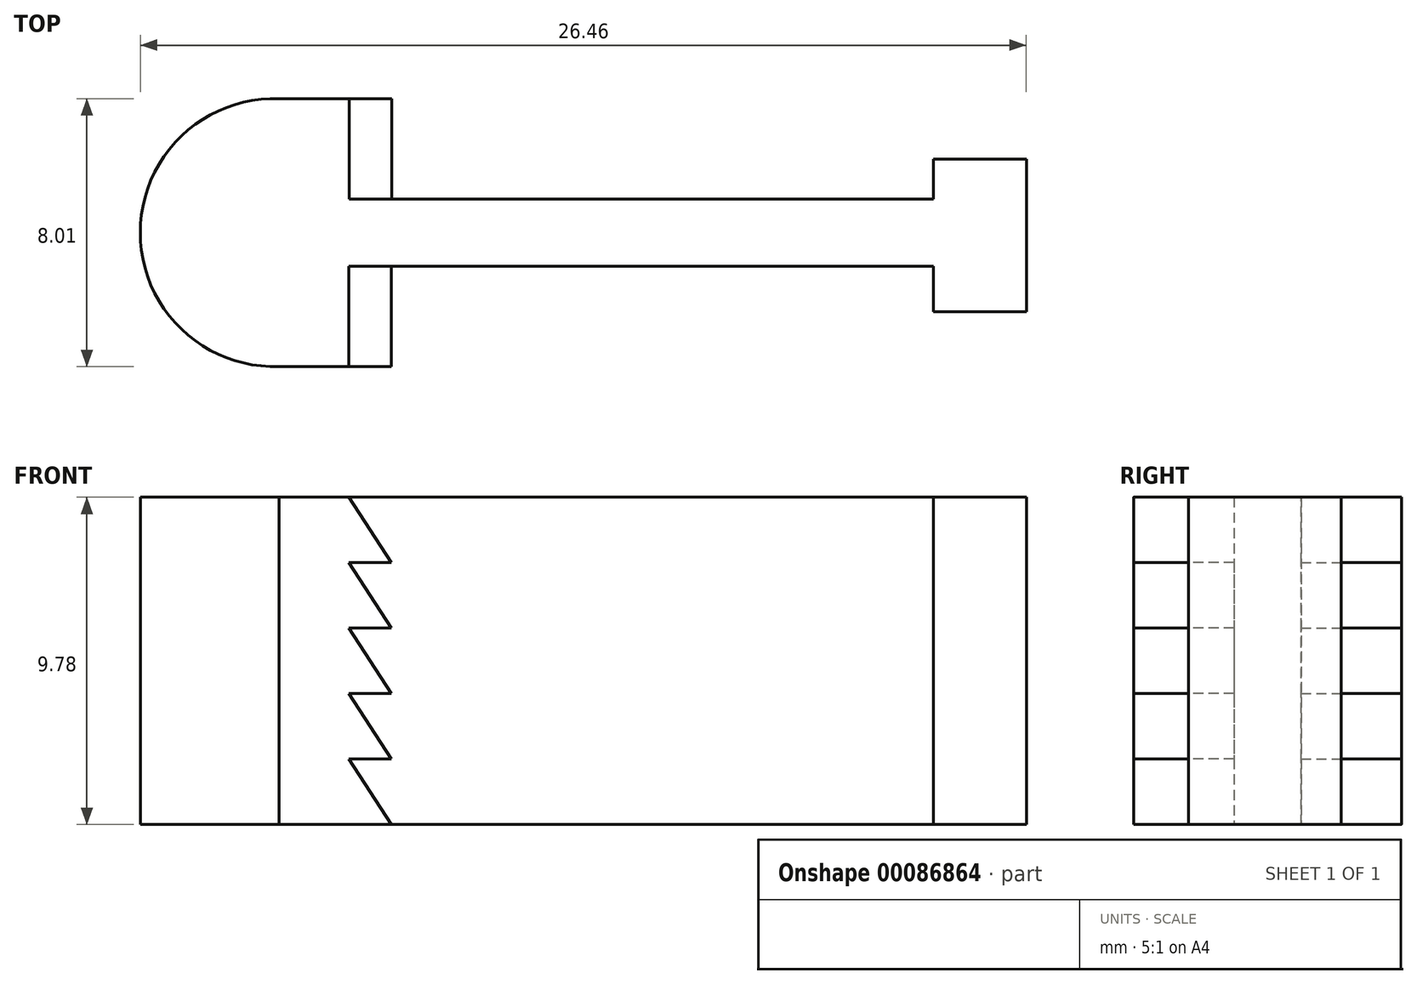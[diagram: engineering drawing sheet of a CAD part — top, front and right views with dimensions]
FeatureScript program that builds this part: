
annotation { "Feature Type Name" : "Feature", "Feature Type Description" : "" }
export const myFeature = defineFeature(function(context is Context, id is Id, definition is map)
    precondition{}
    {
        {
            var Q0;
            Q0=qCreatedBy(makeId("Top.planeOp"),FACE);
            var sketch = newSketch(context, id + "F0", { "sketchPlane" : qUnion([Q0])});
            skLineSegment(sketch, "E0.bottom", {"start": v(-4.73, -0.91) * mm, "end": v(13.05, -0.91) * mm});
            skLineSegment(sketch, "E0.top", {"start": v(-4.73, -2.91) * mm, "end": v(13.05, -2.91) * mm});
            skLineSegment(sketch, "E0.left", {"start": v(-4.73, -0.91) * mm, "end": v(-4.73, -2.91) * mm});
            skLineSegment(sketch, "E0.right", {"start": v(13.05, -0.91) * mm, "end": v(13.05, -2.91) * mm});
            skLineSegment(sketch, "E1.bottom", {"start": v(-4.73, -0.91) * mm, "end": v(-1.23, -0.91) * mm});
            skLineSegment(sketch, "E1.top", {"start": v(-4.73, 2.09) * mm, "end": v(-1.23, 2.09) * mm});
            skLineSegment(sketch, "E1.left", {"start": v(-4.73, -0.91) * mm, "end": v(-4.73, 2.09) * mm});
            skLineSegment(sketch, "E1.right", {"start": v(-1.23, -0.91) * mm, "end": v(-1.23, 2.09) * mm});
            skLineSegment(sketch, "E2.bottom", {"start": v(-4.73, -2.91) * mm, "end": v(-1.23, -2.91) * mm});
            skLineSegment(sketch, "E2.top", {"start": v(-4.73, -5.91) * mm, "end": v(-1.23, -5.91) * mm});
            skLineSegment(sketch, "E2.left", {"start": v(-4.73, -2.91) * mm, "end": v(-4.73, -5.91) * mm});
            skLineSegment(sketch, "E2.right", {"start": v(-1.23, -2.91) * mm, "end": v(-1.23, -5.91) * mm});
            skLineSegment(sketch, "E3.bottom", {"start": v(13.05, -0.91) * mm, "end": v(14.96, -0.91) * mm});
            skLineSegment(sketch, "E3.top", {"start": v(13.05, -2.91) * mm, "end": v(14.96, -2.91) * mm});
            skLineSegment(sketch, "E3.right", {"start": v(14.96, -0.91) * mm, "end": v(14.96, -2.91) * mm});
            skLineSegment(sketch, "E4.bottom", {"start": v(14.96, -4.27) * mm, "end": v(17.73, -4.27) * mm});
            skLineSegment(sketch, "E4.top", {"start": v(14.96, 0.29) * mm, "end": v(17.73, 0.29) * mm});
            skLineSegment(sketch, "E4.left", {"start": v(14.96, -4.27) * mm, "end": v(14.96, 0.29) * mm});
            skLineSegment(sketch, "E4.right", {"start": v(17.73, -4.27) * mm, "end": v(17.73, 0.29) * mm});
            skCircle(sketch, "E5", {"center": v(-4.73, -1.91) * mm, "radius": 4 * mm});
            skSolve(sketch);
        }
        {
            var Q0;
            {var subQ3=sQuery(id+"F0.wireOp",EDGE,"E4.bottom");Q0=makeQuery(id+"F0.imprint","IMPRINT",FACE,{"disambiguationData":[TD([[makeQuery(id+"F0.imprint","IMPRINT",EDGE,{"derivedFrom":subQ3}),1.0]])]});}
            var Q1;
            {var subQ0=sQuery(id+"F0.wireOp",EDGE,"E0.right");Q1=makeQuery(id+"F0.imprint","IMPRINT",FACE,{"disambiguationData":[TD([[makeQuery(id+"F0.imprint","IMPRINT",EDGE,{"derivedFrom":subQ0}),-1.0]])]});}
            var Q2;
            {var subQ0=sQuery(id+"F0.wireOp",EDGE,"E3.bottom");Q2=makeQuery(id+"F0.imprint","IMPRINT",FACE,{"disambiguationData":[TD([[makeQuery(id+"F0.imprint","IMPRINT",EDGE,{"derivedFrom":subQ0}),-1.0]])]});}
            var Q3;
            {var subQ1=sQuery(id+"F0.wireOp",EDGE,"E1.left");var subQ6=sQuery(id+"F0.wireOp",EDGE,"E1.top");var subQ9=makeQuery(id+"F0.imprint","INTERSECT",VERTEX,{"derivedFrom":[subQ6,subQ1]});Q3=makeQuery(id+"F0.imprint","IMPRINT",FACE,{"disambiguationData":[TD([[makeQuery(id+"F0.imprint","IMPRINT",EDGE,{"disambiguationData":[TD([[subQ9,-1.0]])],"derivedFrom":subQ6}),1.0]])]});}
            var Q4;
            {var subQ1=sQuery(id+"F0.wireOp",EDGE,"E2.left");var subQ6=sQuery(id+"F0.wireOp",EDGE,"E2.top");var subQ9=makeQuery(id+"F0.imprint","INTERSECT",VERTEX,{"derivedFrom":[subQ6,subQ1]});Q4=makeQuery(id+"F0.imprint","IMPRINT",FACE,{"disambiguationData":[TD([[makeQuery(id+"F0.imprint","IMPRINT",EDGE,{"disambiguationData":[TD([[subQ9,-1.0]])],"derivedFrom":subQ6}),-1.0]])]});}
            var Q5;
            {var subQ0=sQuery(id+"F0.wireOp",EDGE,"fi6eeUua-WoeC-Sxvv-xVol-Bu5kXO0VCXWT");var subQ1=sQuery(id+"F0.wireOp",EDGE,"E0.bottom");var subQ2=makeQuery(id+"F0.imprint","INTERSECT",VERTEX,{"derivedFrom":[subQ1,subQ0]});Q5=makeQuery(id+"F0.imprint","IMPRINT",FACE,{"disambiguationData":[TD([[makeQuery(id+"F0.imprint","IMPRINT",EDGE,{"disambiguationData":[TD([[subQ2,1.0]])],"derivedFrom":subQ1}),-1.0]])]});}
            var Q6;
            {var subQ0=sQuery(id+"F0.wireOp",EDGE,"E2.bottom");Q6=makeQuery(id+"F0.imprint","IMPRINT",FACE,{"disambiguationData":[TD([[makeQuery(id+"F0.imprint","IMPRINT",EDGE,{"derivedFrom":subQ0}),-1.0]])]});}
            var Q7;
            {var subQ0=sQuery(id+"F0.wireOp",EDGE,"E1.bottom");Q7=makeQuery(id+"F0.imprint","IMPRINT",FACE,{"disambiguationData":[TD([[makeQuery(id+"F0.imprint","IMPRINT",EDGE,{"derivedFrom":subQ0}),1.0]])]});}
            var Q8;
            Q8=makeQuery(id+"F0.imprint","IMPRINT",FACE,{"disambiguationData":[TD([[makeQuery(id+"F0.imprint","IMPRINT",EDGE,{"derivedFrom":sQuery(id+"F0.wireOp",EDGE,"E0.left")}),1.0]])]});
            var Q9;
            {var subQ0=sQuery(id+"F0.wireOp",EDGE,"fi6eeUua-WoeC-Sxvv-xVol-Bu5kXO0VCXWT");var subQ1=sQuery(id+"F0.wireOp",EDGE,"E2.left");var subQ2=makeQuery(id+"F0.imprint","INTERSECT",VERTEX,{"derivedFrom":[subQ1,subQ0]});Q9=makeQuery(id+"F0.imprint","IMPRINT",FACE,{"disambiguationData":[TD([[makeQuery(id+"F0.imprint","IMPRINT",EDGE,{"disambiguationData":[TD([[subQ2,1.0]])],"derivedFrom":subQ1}),-1.0]])]});}
            var Q10;
            {var subQ0=sQuery(id+"F0.wireOp",EDGE,"fi6eeUua-WoeC-Sxvv-xVol-Bu5kXO0VCXWT");var subQ1=sQuery(id+"F0.wireOp",EDGE,"E1.left");var subQ2=makeQuery(id+"F0.imprint","INTERSECT",VERTEX,{"derivedFrom":[subQ1,subQ0]});Q10=makeQuery(id+"F0.imprint","IMPRINT",FACE,{"disambiguationData":[TD([[makeQuery(id+"F0.imprint","IMPRINT",EDGE,{"disambiguationData":[TD([[subQ2,1.0]])],"derivedFrom":subQ1}),1.0]])]});}
            var Q11;
            {var subQ0=sQuery(id+"F0.wireOp",EDGE,"fi6eeUua-WoeC-Sxvv-xVol-Bu5kXO0VCXWT");var subQ1=sQuery(id+"F0.wireOp",EDGE,"E1.left");var subQ2=makeQuery(id+"F0.imprint","INTERSECT",VERTEX,{"derivedFrom":[subQ1,subQ0]});Q11=makeQuery(id+"F0.imprint","IMPRINT",FACE,{"disambiguationData":[TD([[makeQuery(id+"F0.imprint","IMPRINT",EDGE,{"disambiguationData":[TD([[subQ2,1.0]])],"derivedFrom":subQ1}),-1.0]])]});}
            var Q12;
            {var subQ0=sQuery(id+"F0.wireOp",EDGE,"E2.top");Q12=makeQuery(id+"F0.imprint","IMPRINT",FACE,{"disambiguationData":[TD([[makeQuery(id+"F0.imprint","IMPRINT",EDGE,{"derivedFrom":subQ0}),1.0]])]});}
            var Q13;
            {var subQ0=sQuery(id+"F0.wireOp",EDGE,"E1.top");Q13=makeQuery(id+"F0.imprint","IMPRINT",FACE,{"disambiguationData":[TD([[makeQuery(id+"F0.imprint","IMPRINT",EDGE,{"derivedFrom":subQ0}),-1.0]])]});}
            var Q14;
            {var subQ0=sQuery(id+"F0.wireOp",EDGE,"fi6eeUua-WoeC-Sxvv-xVol-Bu5kXO0VCXWT");var subQ1=sQuery(id+"F0.wireOp",EDGE,"E2.left");var subQ2=makeQuery(id+"F0.imprint","INTERSECT",VERTEX,{"derivedFrom":[subQ1,subQ0]});Q14=makeQuery(id+"F0.imprint","IMPRINT",FACE,{"disambiguationData":[TD([[makeQuery(id+"F0.imprint","IMPRINT",EDGE,{"disambiguationData":[TD([[subQ2,1.0]])],"derivedFrom":subQ1}),1.0]])]});}
            var Q15;
            {var subQ0=sQuery(id+"F0.wireOp",EDGE,"E0.left");Q15=makeQuery(id+"F0.imprint","IMPRINT",FACE,{"disambiguationData":[TD([[makeQuery(id+"F0.imprint","IMPRINT",EDGE,{"derivedFrom":subQ0}),-1.0]])]});}
            var Q16;
            {var subQ5=sQuery(id+"F0.wireOp",EDGE,"jR2p0Ju4-ia6Z-jkEp-FwCM-pTLauQKn6Nhj");var subQ7=sQuery(id+"F0.wireOp",EDGE,"E2.left");var subQ8=makeQuery(id+"F0.imprint","INTERSECT",VERTEX,{"derivedFrom":[subQ7,subQ5]});Q16=makeQuery(id+"F0.imprint","IMPRINT",FACE,{"disambiguationData":[TD([[makeQuery(id+"F0.imprint","IMPRINT",EDGE,{"disambiguationData":[TD([[subQ8,-1.0]])],"derivedFrom":subQ7}),1.0]])]});}
            var Q17;
            {var subQ1=sQuery(id+"F0.wireOp",EDGE,"E1.left");var subQ7=sQuery(id+"F0.wireOp",EDGE,"jR2p0Ju4-ia6Z-jkEp-FwCM-pTLauQKn6Nhj");var subQ8=makeQuery(id+"F0.imprint","INTERSECT",VERTEX,{"derivedFrom":[subQ1,subQ7]});Q17=makeQuery(id+"F0.imprint","IMPRINT",FACE,{"disambiguationData":[TD([[makeQuery(id+"F0.imprint","IMPRINT",EDGE,{"disambiguationData":[TD([[subQ8,-1.0]])],"derivedFrom":subQ1}),-1.0]])]});}
            var Q18;
            {var subQ1=sQuery(id+"F0.wireOp",EDGE,"E0.bottom");var subQ9=sQuery(id+"F0.wireOp",EDGE,"E5");var subQ11=makeQuery(id+"F0.imprint","INTERSECT",VERTEX,{"derivedFrom":[subQ1,subQ9]});Q18=makeQuery(id+"F0.imprint","IMPRINT",FACE,{"disambiguationData":[TD([[makeQuery(id+"F0.imprint","IMPRINT",EDGE,{"disambiguationData":[TD([[subQ11,1.0]])],"derivedFrom":subQ9}),1.0]])]});}
            extrude(context, id + "F1", {"entities" : qUnion([Q0, Q1, Q2, Q3, Q4, Q5, Q6, Q7, Q8, Q9, Q10, Q11, Q12, Q13, Q14, Q15, Q16, Q17, Q18]), "depth" : 9.78 * mm});
        }
        {
            var Q0;
            Q0=makeQuery(id+"F1.opExtrude","SWEPT_FACE",FACE,{"disambiguationData":[OSD([sQuery(id+"F0.wireOp",EDGE,"E2.top")])]});
            var sketch = newSketch(context, id + "F2", { "sketchPlane" : qUnion([Q0])});
            skPoint(sketch, "E6.endSnap0", {"position": v(-1.23, 4.89) * mm});
            skLineSegment(sketch, "E7", {"start": v(-2.5, 9.78) * mm, "end": v(-1.23, 9.78) * mm});
            skLineSegment(sketch, "E8", {"start": v(-1.23, 9.78) * mm, "end": v(-1.23, 4.89) * mm});
            skLineSegment(sketch, "E9", {"start": v(-1.23, 4.89) * mm, "end": v(-1.23, 0) * mm});
            skLineSegment(sketch, "E10", {"start": v(-1.23, 1.96) * mm, "end": v(-2.5, 1.96) * mm});
            skLineSegment(sketch, "E11", {"start": v(-1.23, 1.96) * mm, "end": v(-1.23, 0) * mm});
            skLineSegment(sketch, "E12", {"start": v(-2.5, 1.96) * mm, "end": v(-1.23, 0) * mm});
            skLineSegment(sketch, "E13", {"start": v(-1.23, 3.91) * mm, "end": v(-2.5, 3.91) * mm});
            skLineSegment(sketch, "E14", {"start": v(-1.23, 5.87) * mm, "end": v(-2.5, 5.87) * mm});
            skLineSegment(sketch, "E15", {"start": v(-1.23, 7.82) * mm, "end": v(-2.5, 7.82) * mm});
            skLineSegment(sketch, "E16", {"start": v(-2.5, 3.91) * mm, "end": v(-1.23, 1.96) * mm});
            skLineSegment(sketch, "E17", {"start": v(-2.5, 5.87) * mm, "end": v(-1.23, 3.91) * mm});
            skLineSegment(sketch, "E18", {"start": v(-2.5, 7.82) * mm, "end": v(-1.23, 5.87) * mm});
            skLineSegment(sketch, "E19", {"start": v(-2.5, 9.78) * mm, "end": v(-1.23, 7.82) * mm});
            skSolve(sketch);
        }
        {
            var Q0;
            Q0 = qSketchRegion(id + "F2", true);
            extrude(context, id + "F3", {"entities" : qUnion([Q0]), "operationType" : NewBodyOperationType.REMOVE, "oppositeDirection" : true, "depth" : 3 * mm});
        }
        {
            var Q0;
            Q0=makeQuery(id+"F1.opExtrude","SWEPT_FACE",FACE,{"disambiguationData":[OSD([sQuery(id+"F0.wireOp",EDGE,"E1.top")])]});
            var sketch = newSketch(context, id + "F4", { "sketchPlane" : qUnion([Q0])});
            skLineSegment(sketch, "E20", {"start": v(1.23, 0) * mm, "end": v(1.23, 4.89) * mm});
            skLineSegment(sketch, "E21", {"start": v(1.23, 4.89) * mm, "end": v(1.23, 9.78) * mm});
            skLineSegment(sketch, "E22", {"start": v(1.23, 9.78) * mm, "end": v(2.5, 9.78) * mm});
            skLineSegment(sketch, "E23", {"start": v(1.23, 1.96) * mm, "end": v(2.5, 1.96) * mm});
            skLineSegment(sketch, "E24", {"start": v(2.5, 3.91) * mm, "end": v(1.23, 3.91) * mm});
            skLineSegment(sketch, "E25", {"start": v(2.5, 5.87) * mm, "end": v(1.23, 5.87) * mm});
            skLineSegment(sketch, "E26", {"start": v(2.5, 7.82) * mm, "end": v(1.23, 7.82) * mm});
            skLineSegment(sketch, "E27", {"start": v(1.23, 0) * mm, "end": v(2.5, 1.96) * mm});
            skLineSegment(sketch, "E28", {"start": v(1.23, 1.96) * mm, "end": v(2.5, 3.91) * mm});
            skLineSegment(sketch, "E29", {"start": v(1.23, 3.91) * mm, "end": v(2.5, 5.87) * mm});
            skLineSegment(sketch, "E30", {"start": v(1.23, 5.87) * mm, "end": v(2.5, 7.82) * mm});
            skLineSegment(sketch, "E31", {"start": v(1.23, 7.82) * mm, "end": v(2.5, 9.78) * mm});
            skSolve(sketch);
        }
        {
            var Q0;
            Q0 = qSketchRegion(id + "F4", true);
            extrude(context, id + "F5", {"entities" : qUnion([Q0]), "operationType" : NewBodyOperationType.REMOVE, "oppositeDirection" : true, "depth" : 3 * mm});
        }
    });
